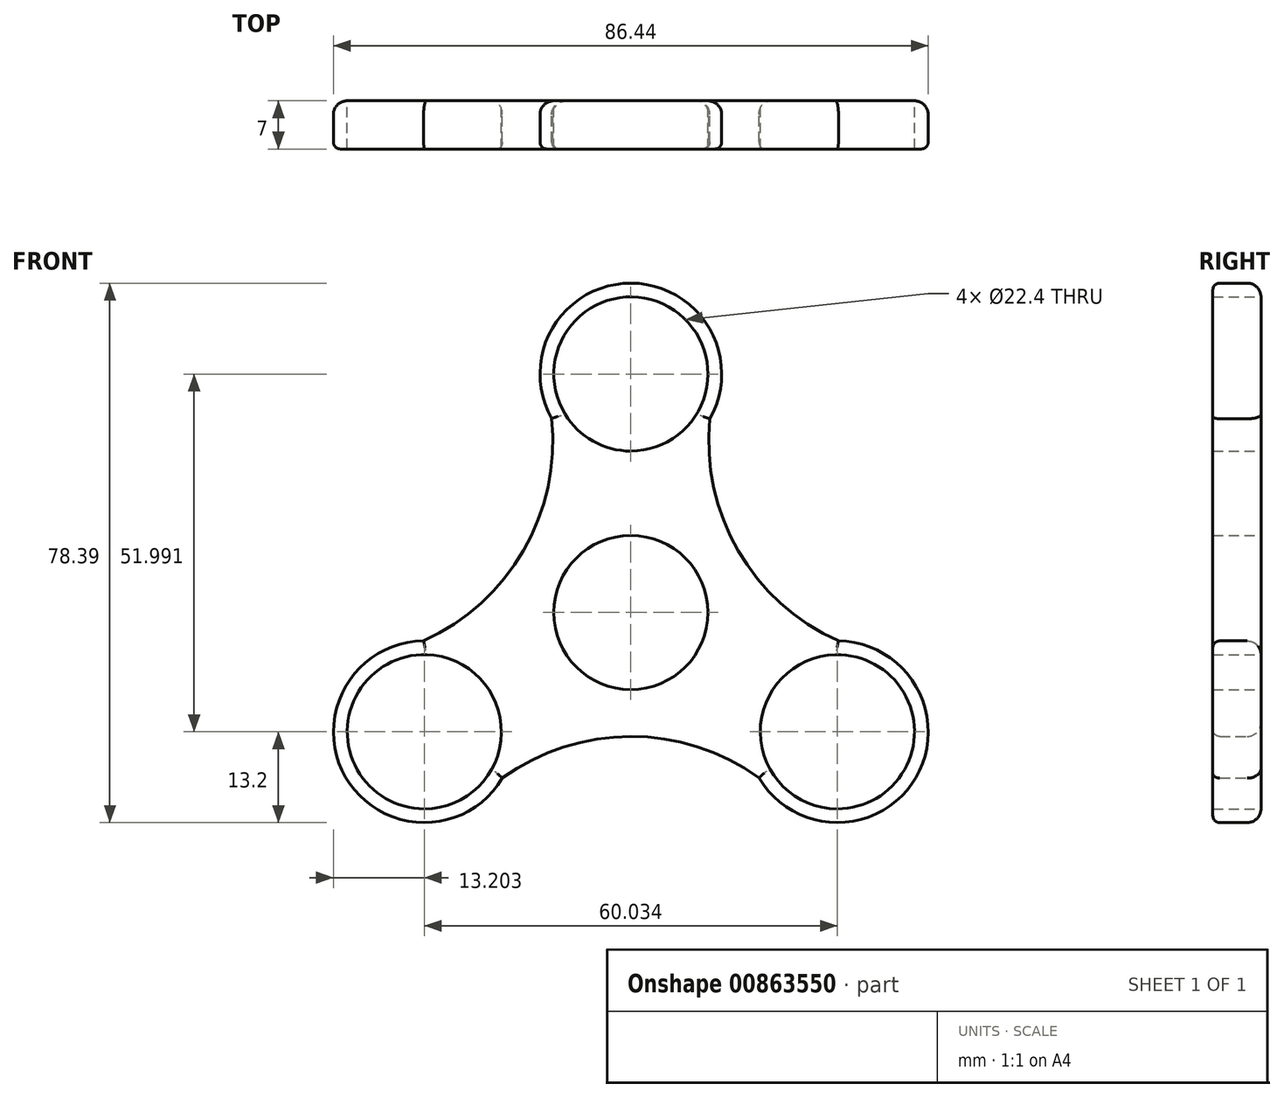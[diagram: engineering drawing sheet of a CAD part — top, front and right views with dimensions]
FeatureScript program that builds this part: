
annotation { "Feature Type Name" : "Feature", "Feature Type Description" : "" }
export const myFeature = defineFeature(function(context is Context, id is Id, definition is map)
    precondition{}
    {
        {
            var Q0;
            Q0=qCreatedBy(makeId("Front.planeOp"),FACE);
            var sketch = newSketch(context, id + "F0", { "sketchPlane" : qUnion([Q0])});
            skCircle(sketch, "E0", {"center": v(0, 0) * mm, "radius": 11.2 * mm});
            skCircle(sketch, "E1", {"center": v(0, 0) * mm, "radius": 13.2 * mm});
            skCircle(sketch, "E2", {"center": v(0, 34.66) * mm, "radius": 11.2 * mm});
            skCircle(sketch, "E3", {"center": v(0, 34.66) * mm, "radius": 13.2 * mm});
            skCircle(sketch, "E4.1.0", {"center": v(-30.02, -17.33) * mm, "radius": 11.2 * mm});
            skCircle(sketch, "E4.1.1", {"center": v(-30.02, -17.33) * mm, "radius": 13.2 * mm});
            skCircle(sketch, "E4.2.0", {"center": v(30.02, -17.33) * mm, "radius": 11.2 * mm});
            skCircle(sketch, "E4.2.1", {"center": v(30.02, -17.33) * mm, "radius": 13.2 * mm});
            skArc(sketch, "E5", {"start": v(-30.12, -4.13) * mm, "mid": v(-15.59, 9.03) * mm, "end": v(-11.51, 28.2) * mm});
            skArc(sketch, "E6.1.0", {"start": v(18.64, -24.02) * mm, "mid": v(-0.02, -18.01) * mm, "end": v(-18.67, -24.07) * mm});
            skArc(sketch, "E6.2.0", {"start": v(11.48, 28.15) * mm, "mid": v(15.61, 8.99) * mm, "end": v(30.18, -4.13) * mm});
            skSolve(sketch);
        }
        {
            var Q0;
            Q0=makeQuery(id+"F0.imprint","IMPRINT",FACE,{"disambiguationData":[TD([[makeQuery(id+"F0.imprint","IMPRINT",EDGE,{"derivedFrom":sQuery(id+"F0.wireOp",EDGE,"E1")}),-1.0]])]});
            var Q1;
            Q1=makeQuery(id+"F0.imprint","IMPRINT",FACE,{"disambiguationData":[TD([[makeQuery(id+"F0.imprint","IMPRINT",EDGE,{"derivedFrom":sQuery(id+"F0.wireOp",EDGE,"E4.1.0")}),-1.0]])]});
            var Q2;
            Q2=makeQuery(id+"F0.imprint","IMPRINT",FACE,{"disambiguationData":[TD([[makeQuery(id+"F0.imprint","IMPRINT",EDGE,{"derivedFrom":sQuery(id+"F0.wireOp",EDGE,"E0")}),-1.0]])]});
            var Q3;
            Q3=makeQuery(id+"F0.imprint","IMPRINT",FACE,{"disambiguationData":[TD([[makeQuery(id+"F0.imprint","IMPRINT",EDGE,{"derivedFrom":sQuery(id+"F0.wireOp",EDGE,"E4.2.0")}),-1.0]])]});
            var Q4;
            Q4=makeQuery(id+"F0.imprint","IMPRINT",FACE,{"disambiguationData":[TD([[makeQuery(id+"F0.imprint","IMPRINT",EDGE,{"derivedFrom":sQuery(id+"F0.wireOp",EDGE,"E2")}),-1.0]])]});
            extrude(context, id + "F1", {"entities" : qUnion([Q0, Q1, Q2, Q3, Q4]), "depth" : 7 * mm, "offsetDistance" : 25 * mm});
        }
        {
            var Q0;
            Q0=makeQuery(id+"F1.opExtrude","CAP_EDGE",EDGE,{"disambiguationData":[OSD([sQuery(id+"F0.wireOp",EDGE,"E5")])],"isStart":false});
            var Q1;
            Q1=makeQuery(id+"F1.opExtrude","CAP_EDGE",EDGE,{"disambiguationData":[OSD([sQuery(id+"F0.wireOp",EDGE,"E3")])],"isStart":false});
            var Q2;
            Q2=makeQuery(id+"F1.opExtrude","CAP_EDGE",EDGE,{"disambiguationData":[OSD([sQuery(id+"F0.wireOp",EDGE,"E6.2.0")])],"isStart":false});
            var Q3;
            Q3=makeQuery(id+"F1.opExtrude","CAP_EDGE",EDGE,{"disambiguationData":[OSD([sQuery(id+"F0.wireOp",EDGE,"E4.2.1")])],"isStart":false});
            var Q4;
            Q4=makeQuery(id+"F1.opExtrude","CAP_EDGE",EDGE,{"disambiguationData":[OSD([sQuery(id+"F0.wireOp",EDGE,"E6.1.0")])],"isStart":false});
            var Q5;
            Q5=makeQuery(id+"F1.opExtrude","CAP_EDGE",EDGE,{"disambiguationData":[OSD([sQuery(id+"F0.wireOp",EDGE,"E4.1.1")])],"isStart":false});
            fillet(context, id + "F2", {"entities" : qUnion([Q0, Q1, Q2, Q3, Q4, Q5]), "radius" : 1 * mm, "tangentPropagation" : true, "allowEdgeOverflow" : false});
        }
        {
            var Q0;
            Q0=makeQuery(id+"F1.opExtrude","CAP_EDGE",EDGE,{"disambiguationData":[OSD([sQuery(id+"F0.wireOp",EDGE,"E4.1.1")])],"isStart":true});
            var Q1;
            Q1=makeQuery(id+"F1.opExtrude","CAP_EDGE",EDGE,{"disambiguationData":[OSD([sQuery(id+"F0.wireOp",EDGE,"E5")])],"isStart":true});
            var Q2;
            Q2=makeQuery(id+"F1.opExtrude","CAP_EDGE",EDGE,{"disambiguationData":[OSD([sQuery(id+"F0.wireOp",EDGE,"E3")])],"isStart":true});
            var Q3;
            Q3=makeQuery(id+"F1.opExtrude","CAP_EDGE",EDGE,{"disambiguationData":[OSD([sQuery(id+"F0.wireOp",EDGE,"E6.2.0")])],"isStart":true});
            var Q4;
            Q4=makeQuery(id+"F1.opExtrude","CAP_EDGE",EDGE,{"disambiguationData":[OSD([sQuery(id+"F0.wireOp",EDGE,"E4.2.1")])],"isStart":true});
            var Q5;
            Q5=makeQuery(id+"F1.opExtrude","CAP_EDGE",EDGE,{"disambiguationData":[OSD([sQuery(id+"F0.wireOp",EDGE,"E6.1.0")])],"isStart":true});
            fillet(context, id + "F3", {"entities" : qUnion([Q0, Q1, Q2, Q3, Q4, Q5]), "radius" : 2 * mm, "tangentPropagation" : true, "allowEdgeOverflow" : false});
        }
    });
